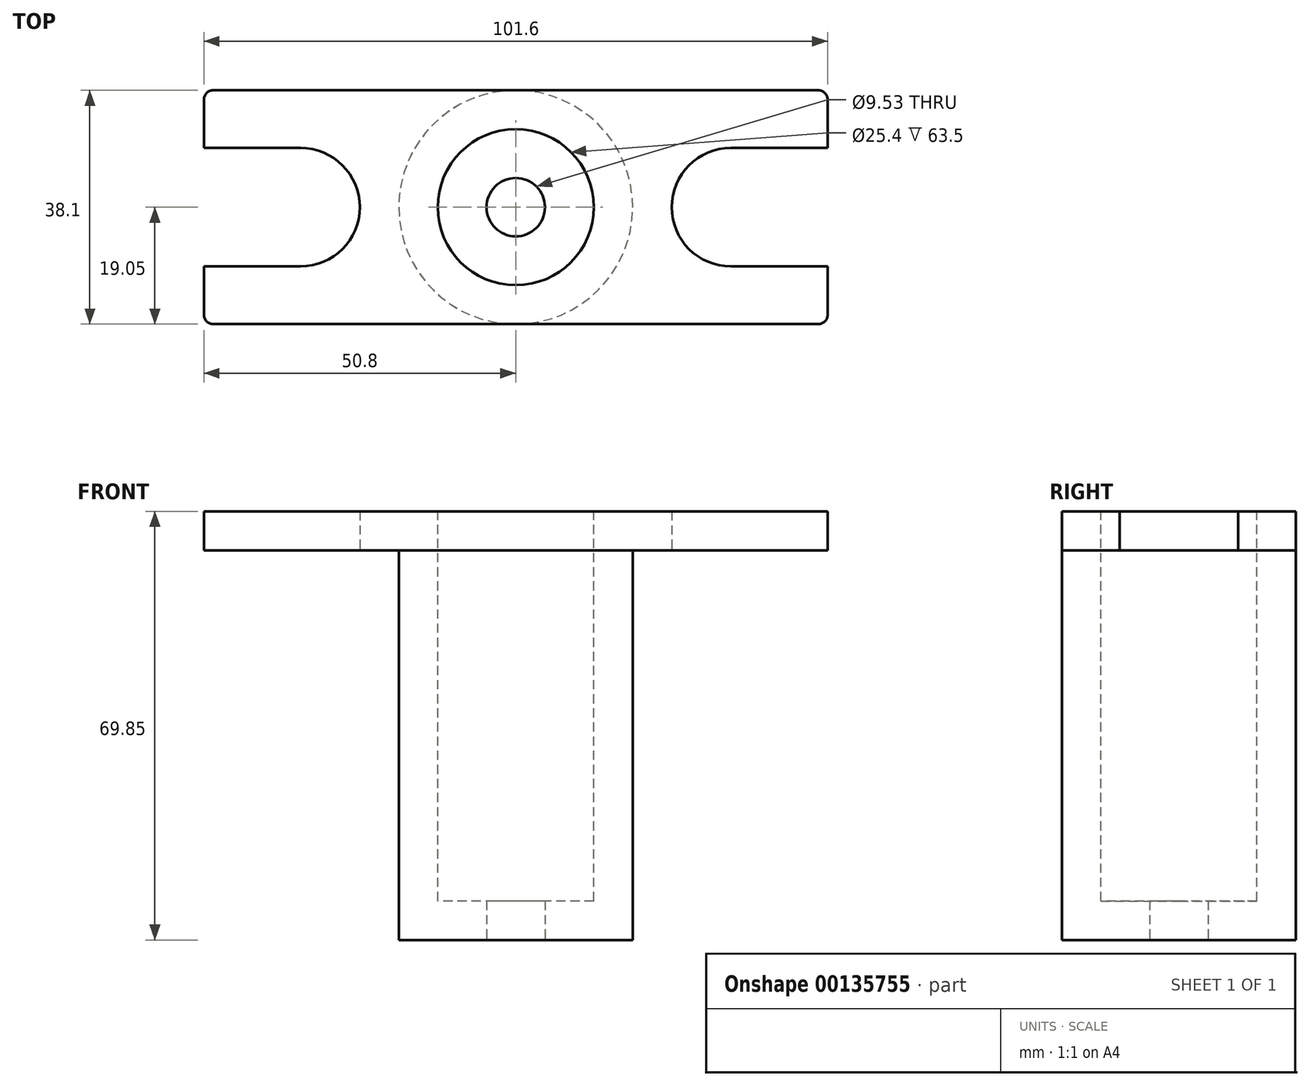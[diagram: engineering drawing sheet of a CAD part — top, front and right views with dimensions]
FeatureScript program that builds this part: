
annotation { "Feature Type Name" : "Feature", "Feature Type Description" : "" }
export const myFeature = defineFeature(function(context is Context, id is Id, definition is map)
    precondition{}
    {
        {
            var Q0;
            Q0=qCreatedBy(makeId("Top.planeOp"),FACE);
            var sketch = newSketch(context, id + "F0", { "sketchPlane" : qUnion([Q0])});
            skLineSegment(sketch, "E0.bottom", {"start": v(-50.8, 19.05) * mm, "end": v(50.8, 19.05) * mm});
            skLineSegment(sketch, "E0.top", {"start": v(-50.8, -19.05) * mm, "end": v(50.8, -19.05) * mm});
            skLineSegment(sketch, "E0.left", {"start": v(-50.8, 19.05) * mm, "end": v(-50.8, 9.65) * mm});
            skLineSegment(sketch, "E0.right", {"start": v(50.8, 19.05) * mm, "end": v(50.8, 9.65) * mm});
            skLineSegment(sketch, "E1", {"start": v(-51.21, 0) * mm, "end": v(57.38, 0) * mm, "construction": true});
            skLineSegment(sketch, "E2", {"start": v(50.8, 9.65) * mm, "end": v(35.05, 9.65) * mm});
            skLineSegment(sketch, "E3", {"start": v(50.8, -9.65) * mm, "end": v(35.05, -9.65) * mm});
            skLineSegment(sketch, "E4", {"start": v(-50.8, 9.65) * mm, "end": v(-35.05, 9.65) * mm});
            skLineSegment(sketch, "E5", {"start": v(-50.8, -9.65) * mm, "end": v(-35.05, -9.65) * mm});
            skArc(sketch, "E6", {"start": v(-35.05, -9.65) * mm, "mid": v(-25.4, 0) * mm, "end": v(-35.05, 9.65) * mm});
            skArc(sketch, "E7", {"start": v(35.05, 9.65) * mm, "mid": v(25.4, 0) * mm, "end": v(35.05, -9.65) * mm});
            skLineSegment(sketch, "E8.trimOffspring", {"start": v(-50.8, -9.65) * mm, "end": v(-50.8, -19.05) * mm});
            skLineSegment(sketch, "E9.trimOffspring", {"start": v(50.8, -9.65) * mm, "end": v(50.8, -19.05) * mm});
            skSolve(sketch);
        }
        {
            var Q0;
            Q0 = qSketchRegion(id + "F0", true);
            extrude(context, id + "F1", {"entities" : qUnion([Q0]), "depth" : 6.35 * mm});
        }
        {
            var Q0;
            Q0=makeQuery(id+"F1.opExtrude","SWEPT_EDGE",EDGE,{"disambiguationData":[OSD([sQuery(id+"F0.wireOp",EDGE,"E0.bottom"),sQuery(id+"F0.wireOp",EDGE,"E0.left")])]});
            var Q1;
            Q1=makeQuery(id+"F1.opExtrude","SWEPT_EDGE",EDGE,{"disambiguationData":[OSD([sQuery(id+"F0.wireOp",EDGE,"E0.top"),sQuery(id+"F0.wireOp",EDGE,"E8.trimOffspring")])]});
            var Q2;
            Q2=makeQuery(id+"F1.opExtrude","SWEPT_EDGE",EDGE,{"disambiguationData":[OSD([sQuery(id+"F0.wireOp",EDGE,"E0.top"),sQuery(id+"F0.wireOp",EDGE,"E9.trimOffspring")])]});
            var Q3;
            Q3=makeQuery(id+"F1.opExtrude","SWEPT_EDGE",EDGE,{"disambiguationData":[OSD([sQuery(id+"F0.wireOp",EDGE,"E0.bottom"),sQuery(id+"F0.wireOp",EDGE,"E0.right")])]});
            fillet(context, id + "F2", {"entities" : qUnion([Q0, Q1, Q2, Q3]), "radius" : 1.52 * mm, "tangentPropagation" : true, "allowEdgeOverflow" : false});
        }
        {
            var Q0;
            Q0=makeQuery(id+"F1.opExtrude","CAP_FACE",FACE,{"disambiguationData":[OSD([sQuery(id+"F0.wireOp",EDGE,"E0.bottom"),sQuery(id+"F0.wireOp",EDGE,"E0.top"),sQuery(id+"F0.wireOp",EDGE,"E0.left"),sQuery(id+"F0.wireOp",EDGE,"E0.right"),sQuery(id+"F0.wireOp",EDGE,"E2"),sQuery(id+"F0.wireOp",EDGE,"E3"),sQuery(id+"F0.wireOp",EDGE,"E4"),sQuery(id+"F0.wireOp",EDGE,"E5"),sQuery(id+"F0.wireOp",EDGE,"E6"),sQuery(id+"F0.wireOp",EDGE,"E7"),sQuery(id+"F0.wireOp",EDGE,"E8.trimOffspring"),sQuery(id+"F0.wireOp",EDGE,"E9.trimOffspring")])],"isStart":true});
            var sketch = newSketch(context, id + "F3", { "sketchPlane" : qUnion([Q0])});
            skCircle(sketch, "E10", {"center": v(0, 0) * mm, "radius": 19.05 * mm});
            skSolve(sketch);
        }
        {
            var Q0;
            Q0 = qSketchRegion(id + "F3", true);
            extrude(context, id + "F4", {"entities" : qUnion([Q0]), "operationType" : NewBodyOperationType.ADD, "depth" : 63.5 * mm});
        }
        {
            var Q0;
            Q0=makeQuery(id+"F4.opExtrude","CAP_FACE",FACE,{"disambiguationData":[OSD([sQuery(id+"F3.wireOp",EDGE,"E10")])],"isStart":false});
            var sketch = newSketch(context, id + "F5", { "sketchPlane" : qUnion([Q0])});
            skCircle(sketch, "E11", {"center": v(0, 0) * mm, "radius": 4.76 * mm});
            skSolve(sketch);
        }
        {
            var Q0;
            Q0=makeQuery(id+"F5.imprint","IMPRINT",FACE,{"disambiguationData":[TD([[makeQuery(id+"F5.imprint","IMPRINT",EDGE,{"derivedFrom":sQuery(id+"F5.wireOp",EDGE,"E11")}),1.0]])]});
            extrude(context, id + "F6", {"entities" : qUnion([Q0]), "operationType" : NewBodyOperationType.REMOVE, "endBound" : BoundingType.THROUGH_ALL, "oppositeDirection" : true, "depth" : 25.4 * mm});
        }
        {
            var Q0;
            Q0=makeQuery(id+"F1.opExtrude","CAP_FACE",FACE,{"disambiguationData":[OSD([sQuery(id+"F0.wireOp",EDGE,"E0.bottom"),sQuery(id+"F0.wireOp",EDGE,"E0.top"),sQuery(id+"F0.wireOp",EDGE,"E0.left"),sQuery(id+"F0.wireOp",EDGE,"E0.right"),sQuery(id+"F0.wireOp",EDGE,"E2"),sQuery(id+"F0.wireOp",EDGE,"E3"),sQuery(id+"F0.wireOp",EDGE,"E4"),sQuery(id+"F0.wireOp",EDGE,"E5"),sQuery(id+"F0.wireOp",EDGE,"E6"),sQuery(id+"F0.wireOp",EDGE,"E7"),sQuery(id+"F0.wireOp",EDGE,"E8.trimOffspring"),sQuery(id+"F0.wireOp",EDGE,"E9.trimOffspring")])],"isStart":false});
            var sketch = newSketch(context, id + "F7", { "sketchPlane" : qUnion([Q0])});
            skCircle(sketch, "E12", {"center": v(0, 0) * mm, "radius": 12.7 * mm});
            skSolve(sketch);
        }
        {
            var Q0;
            Q0 = qSketchRegion(id + "F7", true);
            extrude(context, id + "F8", {"entities" : qUnion([Q0]), "operationType" : NewBodyOperationType.REMOVE, "oppositeDirection" : true, "depth" : 63.5 * mm});
        }
    });
